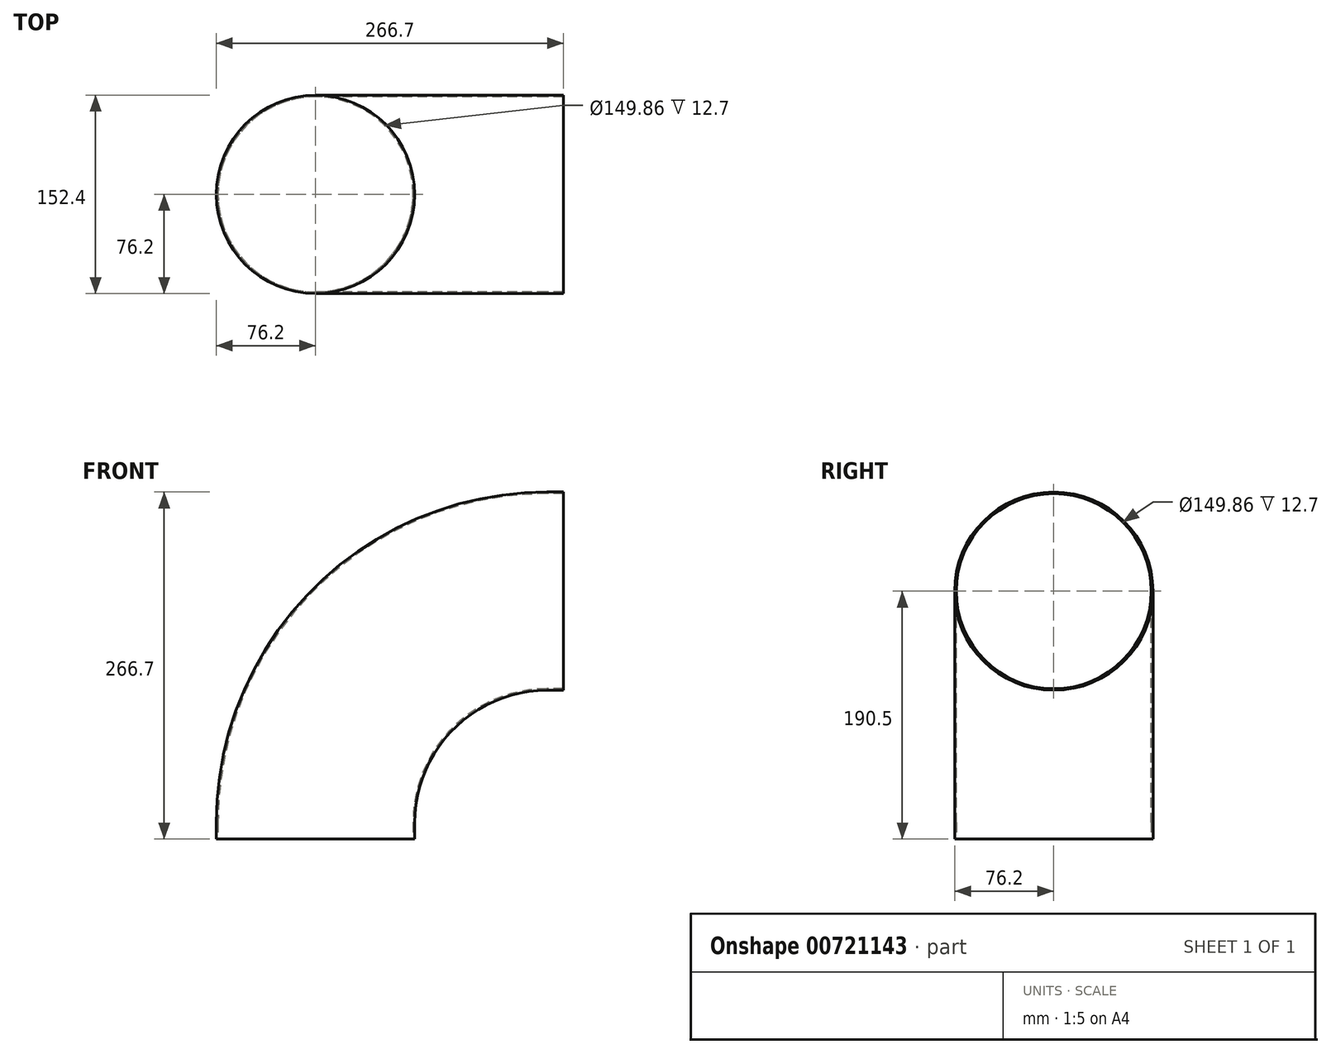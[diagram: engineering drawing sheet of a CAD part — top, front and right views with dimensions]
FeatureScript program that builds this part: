
annotation { "Feature Type Name" : "Feature", "Feature Type Description" : "" }
export const myFeature = defineFeature(function(context is Context, id is Id, definition is map)
    precondition{}
    {
        {
            var Q0;
            Q0=qCreatedBy(makeId("Top.planeOp"),FACE);
            var sketch = newSketch(context, id + "F0", { "sketchPlane" : qUnion([Q0])});
            skCircle(sketch, "E0", {"center": v(0, 0) * mm, "radius": 74.93 * mm});
            skCircle(sketch, "E1", {"center": v(0, 0) * mm, "radius": 76.2 * mm});
            skSolve(sketch);
        }
        {
            var Q0;
            Q0=makeQuery(id+"F0.imprint","IMPRINT",FACE,{"disambiguationData":[TD([[makeQuery(id+"F0.imprint","IMPRINT",EDGE,{"derivedFrom":sQuery(id+"F0.wireOp",EDGE,"E0")}),-1.0]])]});
            extrude(context, id + "F1", {"entities" : qUnion([Q0]), "depth" : 12.7 * mm, "offsetDistance" : 25.4 * mm});
        }
        {
            var Q0;
            Q0=makeQuery(id+"F1.opExtrude","CAP_FACE",FACE,{"disambiguationData":[OSD([sQuery(id+"F0.wireOp",EDGE,"E0"),sQuery(id+"F0.wireOp",EDGE,"E1")])],"isStart":false});
            var sketch = newSketch(context, id + "F2", { "sketchPlane" : qUnion([Q0])});
            skLineSegment(sketch, "E2", {"start": v(177.8, -27.25) * mm, "end": v(177.8, 21.39) * mm, "construction": true});
            skSolve(sketch);
        }
        {
            var Q0;
            Q0=makeQuery(id+"F2.imprint","IMPRINT",FACE,{"disambiguationData":[TD([[makeQuery(id+"F2.imprint","IMPRINT",EDGE,{"derivedFrom":makeQuery(id+"F1.opExtrude","CAP_EDGE",EDGE,{"disambiguationData":[OSD([sQuery(id+"F0.wireOp",EDGE,"E0")])],"isStart":false})}),-1.0]])]});
            var Q1;
            Q1=sQuery(id+"F2.wireOp",EDGE,"E2");
            revolve(context, id + "F3", {"operationType" : NewBodyOperationType.ADD, "entities" : qUnion([Q0]), "axis" : qUnion([Q1]), "revolveType" : RevolveType.ONE_DIRECTION, "angle" : 90 * degree});
        }
        {
            var Q0;
            Q0=makeQuery(id+"F3.opRevolve","CAP_FACE",FACE,{"disambiguationData":[OSD([sQuery(id+"F0.wireOp",EDGE,"E0"),sQuery(id+"F0.wireOp",EDGE,"E1")])],"isStart":false});
            extrude(context, id + "F4", {"entities" : qUnion([Q0]), "operationType" : NewBodyOperationType.ADD, "depth" : 12.7 * mm});
        }
    });
